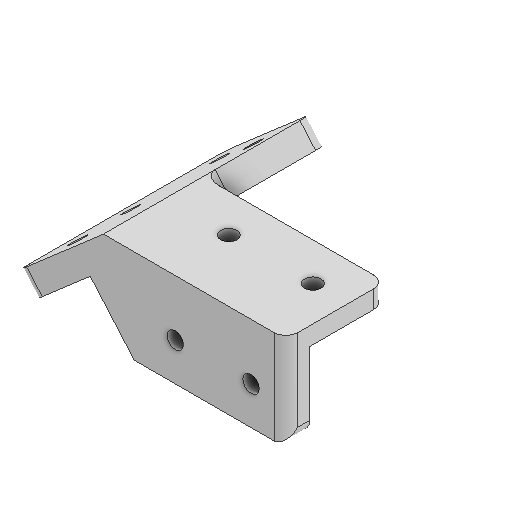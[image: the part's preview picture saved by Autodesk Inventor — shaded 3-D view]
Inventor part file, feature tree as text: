
AUTODESK INVENTOR PART (.ipt)
format: ipt  version: 2025 (Build 290162000, 162)  size: 199,168 bytes
history: native  units: mm
features: reference x7, extrude x5, sketch x5, other x5, projected_geometry x4, fillet x2, mirror x1
ambient origin geometry x8: Origin, YZ Plane, XZ Plane, XY Plane, X Axis, Y Axis, Z Axis, Center Point
bodies: Solid1 (feature_tree)
feature tree (29):
  extrude  "Extrusion1"  Depth=50.8mm
  extrude  "Extrusion2"  Depth=5.5mm
  extrude  "Extrusion3"  Depth=8.0mm TaperAngle=0.0deg
  extrude  "Extrusion4"  Depth=33.4mm
  extrude  "Extrusion5"  Depth=8.0mm TaperAngle=0.0deg
  fillet  "Fillet1"  [1 undecoded]
  fillet  "Fillet2"  Radius=2.0mm
  mirror  "Mirror1"
  sketch  "Sketch1"  dims[d0=25.4mm d1=50.8mm]
  sketch  "Sketch2"  dims[d2=5.5mm d3=5.5mm]
  projected_geometry  "Projected Loop1"
  reference  "Reference1"
  sketch  "Sketch3"  dims[d4=25.4mm d5=8.0mm d6=0.0mm]
  reference  "Reference2"
  reference  "Reference3"
  projected_geometry  "Projected Loop2"
  reference  "Reference4"
  reference  "Reference5"
  reference  "Reference6"
  reference  "Reference7"
  sketch  "Sketch4"  dims[d7=33.4mm d8=0.0mm d9=5.5mm]
  projected_geometry  "Projected Loop3"
  sketch  "Sketch5"  dims[d10=8.0mm d11=0.0mm d12=8.0mm d13=0.0mm d14=0.0mm d15=0.0mm d16=2.0mm d17=4.0mm]
  projected_geometry  "Projected Loop4"
  other  "<userpath>\Desktop\puppycat\woodhouseMK1.iam"
  other  "woodhouseMK1.iam"
  other  "swingarmBaseV4:1"
  other  "horizontalStrut:1"
  other  "trackBase:1"
note: 1 required parameter value undecoded (feature->parameter linkage not recoverable at this tier; creation-order binding heuristic only, values carry confidence <= 0.55)
